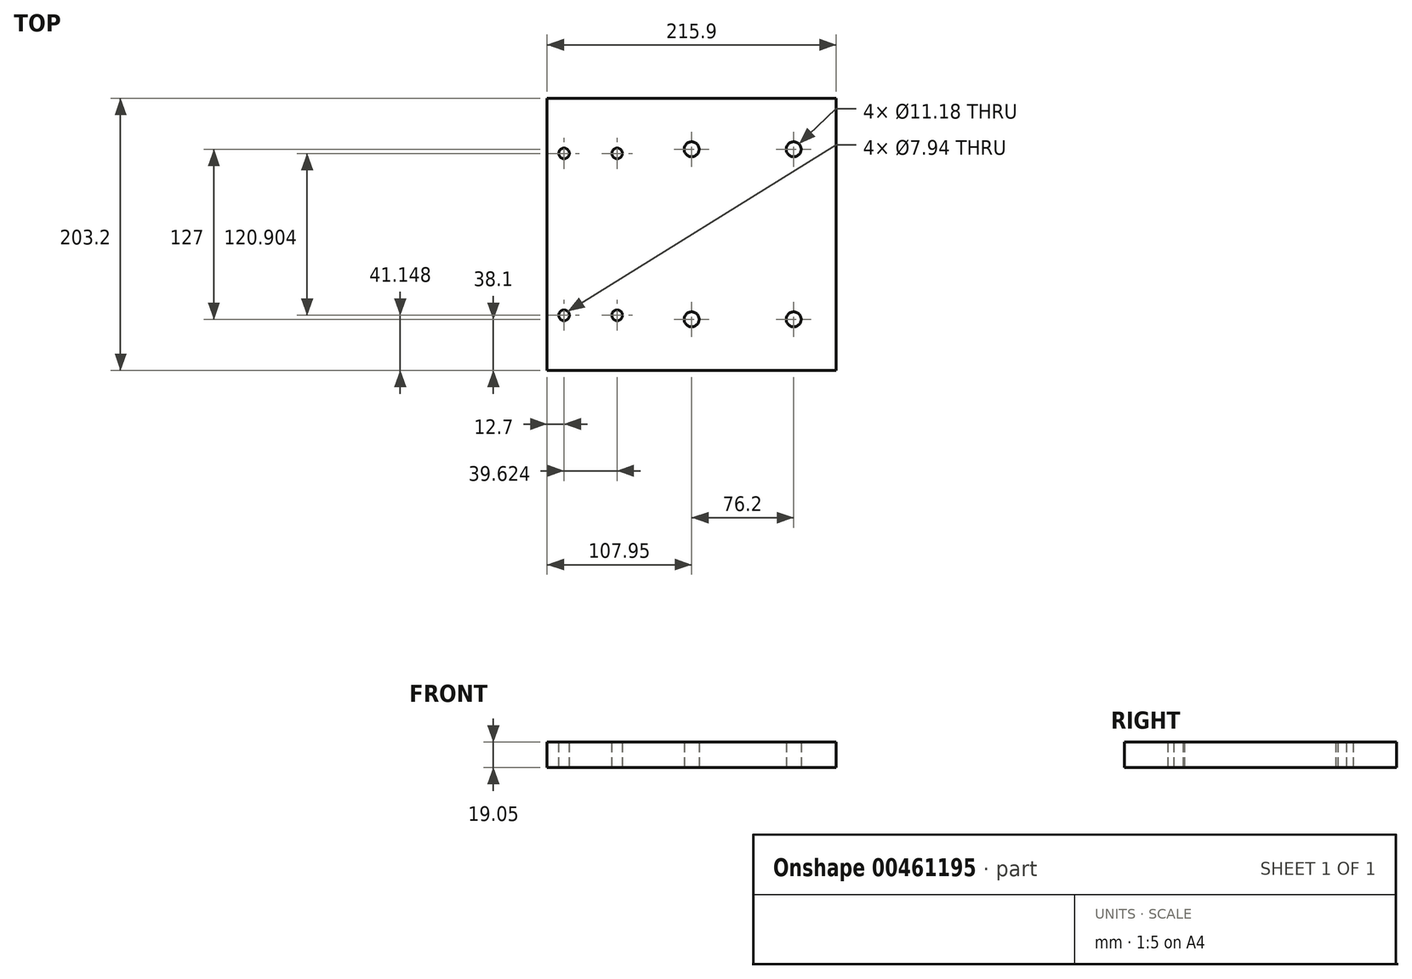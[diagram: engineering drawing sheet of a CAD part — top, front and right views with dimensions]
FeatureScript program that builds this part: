
annotation { "Feature Type Name" : "Feature", "Feature Type Description" : "" }
export const myFeature = defineFeature(function(context is Context, id is Id, definition is map)
    precondition{}
    {
        {
            var Q0;
            Q0=qCreatedBy(makeId("Top.planeOp"),FACE);
            var sketch = newSketch(context, id + "F0", { "sketchPlane" : qUnion([Q0])});
            skLineSegment(sketch, "E0.bottom", {"start": v(-107.95, 101.6) * mm, "end": v(107.95, 101.6) * mm});
            skLineSegment(sketch, "E0.top", {"start": v(-107.95, -101.6) * mm, "end": v(107.95, -101.6) * mm});
            skLineSegment(sketch, "E0.left", {"start": v(-107.95, 101.6) * mm, "end": v(-107.95, -101.6) * mm});
            skLineSegment(sketch, "E0.right", {"start": v(107.95, 101.6) * mm, "end": v(107.95, -101.6) * mm});
            skPoint(sketch, "E0.middle", {"position": v(0, 0) * mm});
            skLineSegment(sketch, "E1.0", {"start": v(38.1, 101.6) * mm, "end": v(38.1, -101.6) * mm, "construction": true});
            skLineSegment(sketch, "E2.0", {"start": v(0, 101.6) * mm, "end": v(0, -101.6) * mm, "construction": true});
            skLineSegment(sketch, "E3", {"start": v(-136.26, 0) * mm, "end": v(140.71, 0) * mm, "construction": true});
            skLineSegment(sketch, "E4.0", {"start": v(-136.26, -63.5) * mm, "end": v(140.71, -63.5) * mm, "construction": true});
            skPoint(sketch, "E5", {"position": v(0, -63.5) * mm});
            skPoint(sketch, "E6.MirrorP", {"position": v(0, 63.5) * mm});
            skPoint(sketch, "E7.MirrorP", {"position": v(76.2, 63.5) * mm});
            skPoint(sketch, "E8.MirrorP", {"position": v(76.2, -63.5) * mm});
            skSolve(sketch);
        }
        {
            var Q0;
            Q0 = qSketchRegion(id + "F0", true);
            extrude(context, id + "F1", {"entities" : qUnion([Q0]), "depth" : 19.05 * mm});
        }
        {
            var Q0;
            Q0=sQuery(id+"F0.wireOp",VERTEX,"E6.MirrorP");
            var Q1;
            Q1=sQuery(id+"F0.wireOp",VERTEX,"E7.MirrorP");
            var Q2;
            Q2=sQuery(id+"F0.wireOp",VERTEX,"E5");
            var Q3;
            Q3=sQuery(id+"F0.wireOp",VERTEX,"E8.MirrorP");
            var Q4;
            Q4=makeQuery(id+"F1.opExtrude","SWEPT_BODY",BODY,{"disambiguationData":[OSD([sQuery(id+"F0.wireOp",EDGE,"E0.bottom"),sQuery(id+"F0.wireOp",EDGE,"E0.top"),sQuery(id+"F0.wireOp",EDGE,"E0.left"),sQuery(id+"F0.wireOp",EDGE,"E0.right")])]});
            hole(context, id + "F2", {"style" : HoleStyle.SIMPLE, "endStyle" : HoleEndStyle.THROUGH, "oppositeDirection" : true, "holeDiameter" : 11.18 * mm, "isTappedThrough" : true, "tappedDepth" : 12.06 * mm, "tapClearance" : 3, "startFromSketch" : true, "locations" : qUnion([Q0, Q1, Q2, Q3]), "scope" : qUnion([Q4])});
        }
        {
            var Q0;
            Q0=makeQuery(id+"F1.opExtrude","CAP_FACE",FACE,{"disambiguationData":[OSD([sQuery(id+"F0.wireOp",EDGE,"E0.bottom"),sQuery(id+"F0.wireOp",EDGE,"E0.top"),sQuery(id+"F0.wireOp",EDGE,"E0.left"),sQuery(id+"F0.wireOp",EDGE,"E0.right")])],"isStart":false});
            var sketch = newSketch(context, id + "F3", { "sketchPlane" : qUnion([Q0])});
            skLineSegment(sketch, "E9.0", {"start": v(-95.25, 101.6) * mm, "end": v(-95.25, -101.6) * mm, "construction": true});
            skLineSegment(sketch, "E10.0", {"start": v(-55.63, 101.6) * mm, "end": v(-55.63, -101.6) * mm, "construction": true});
            skLineSegment(sketch, "E11.0", {"start": v(-136.26, 0) * mm, "end": v(140.71, 0) * mm, "construction": true});
            skLineSegment(sketch, "E12.0", {"start": v(-136.26, -60.45) * mm, "end": v(140.71, -60.45) * mm, "construction": true});
            skPoint(sketch, "E13", {"position": v(-95.25, -60.45) * mm});
            skPoint(sketch, "E14", {"position": v(-55.63, -60.45) * mm});
            skPoint(sketch, "E15.MirrorP", {"position": v(-95.25, 60.45) * mm});
            skPoint(sketch, "E16.MirrorP", {"position": v(-55.63, 60.45) * mm});
            skSolve(sketch);
        }
        {
            var Q0;
            Q0=sQuery(id+"F3.wireOp",VERTEX,"E15.MirrorP");
            var Q1;
            Q1=sQuery(id+"F3.wireOp",VERTEX,"E16.MirrorP");
            var Q2;
            Q2=sQuery(id+"F3.wireOp",VERTEX,"E13");
            var Q3;
            Q3=sQuery(id+"F3.wireOp",VERTEX,"E14");
            var Q4;
            Q4=makeQuery(id+"F1.opExtrude","SWEPT_BODY",BODY,{"disambiguationData":[OSD([sQuery(id+"F0.wireOp",EDGE,"E0.bottom"),sQuery(id+"F0.wireOp",EDGE,"E0.top"),sQuery(id+"F0.wireOp",EDGE,"E0.left"),sQuery(id+"F0.wireOp",EDGE,"E0.right")])]});
            hole(context, id + "F4", {"style" : HoleStyle.SIMPLE, "endStyle" : HoleEndStyle.THROUGH, "standardTappedOrClearance" : lookupTablePath({ "standard" : "ANSI", "engagement" : "75%", "pitch" : "16 tpi", "size" : "3/8", "type" : "Tapped" }), "standardBlindInLast" : lookupTablePath({ "standard" : "ANSI", "engagement" : "75%", "pitch" : "16 tpi", "size" : "3/8", "type" : "Tapped" }), "holeDiameter" : 7.94 * mm, "showTappedDepth" : true, "isTappedThrough" : true, "tappedDepth" : 12.06 * mm, "tapClearance" : 3, "startFromSketch" : true, "locations" : qUnion([Q0, Q1, Q2, Q3]), "scope" : qUnion([Q4]), "majorDiameter" : 9.53 * mm});
        }
    });
